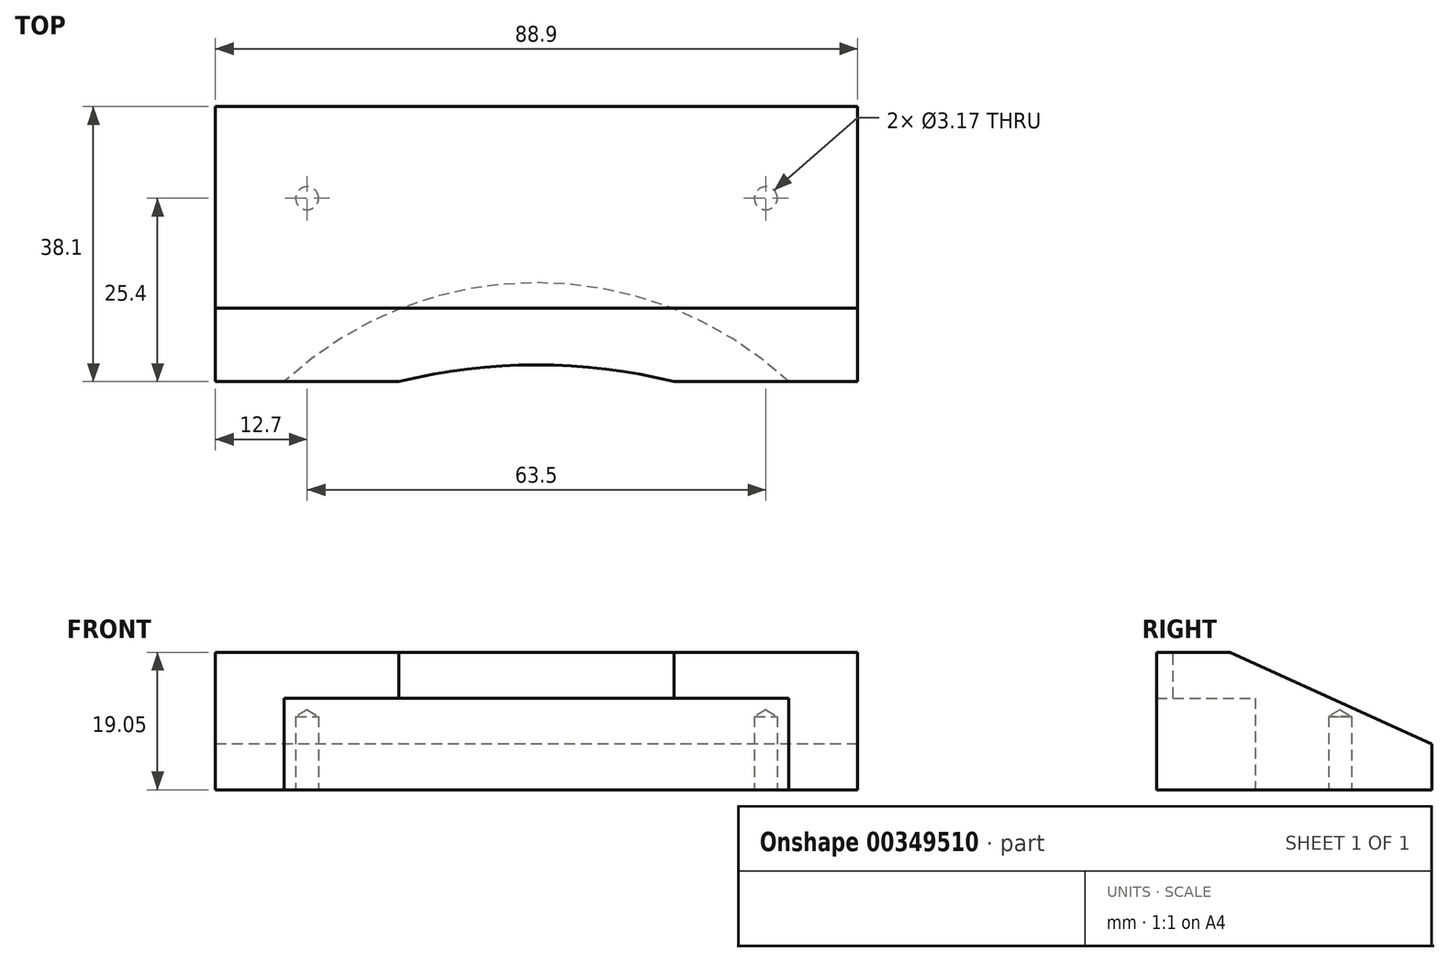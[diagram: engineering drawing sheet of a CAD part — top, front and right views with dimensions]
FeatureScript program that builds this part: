
annotation { "Feature Type Name" : "Feature", "Feature Type Description" : "" }
export const myFeature = defineFeature(function(context is Context, id is Id, definition is map)
    precondition{}
    {
        {
            var Q0;
            Q0=qCreatedBy(makeId("Top.planeOp"),FACE);
            var sketch = newSketch(context, id + "F0", { "sketchPlane" : qUnion([Q0])});
            skLineSegment(sketch, "E0.bottom", {"start": v(44.45, 19.05) * mm, "end": v(-44.45, 19.05) * mm});
            skLineSegment(sketch, "E0.top", {"start": v(44.45, -19.05) * mm, "end": v(-44.45, -19.05) * mm});
            skLineSegment(sketch, "E0.left", {"start": v(44.45, 19.05) * mm, "end": v(44.45, -19.05) * mm});
            skLineSegment(sketch, "E0.right", {"start": v(-44.45, 19.05) * mm, "end": v(-44.45, -19.05) * mm});
            skPoint(sketch, "E0.middle", {"position": v(0, 0) * mm});
            skSolve(sketch);
        }
        {
            var Q0;
            Q0=makeQuery(id+"F0.imprint","IMPRINT",FACE,{"disambiguationData":[TD([[makeQuery(id+"F0.imprint","IMPRINT",EDGE,{"derivedFrom":sQuery(id+"F0.wireOp",EDGE,"E0.bottom")}),1.0]])]});
            extrude(context, id + "F1", {"entities" : qUnion([Q0]), "depth" : 19.05 * mm});
        }
        {
            var Q0;
            Q0=makeQuery(id+"F1.opExtrude","SWEPT_FACE",FACE,{"disambiguationData":[OSD([sQuery(id+"F0.wireOp",EDGE,"E0.right")])]});
            var sketch = newSketch(context, id + "F2", { "sketchPlane" : qUnion([Q0])});
            skLineSegment(sketch, "E1", {"start": v(-19.05, 0) * mm, "end": v(-19.05, 6.35) * mm});
            skLineSegment(sketch, "E2", {"start": v(19.05, 19.05) * mm, "end": v(8.9, 19.05) * mm});
            skLineSegment(sketch, "E3", {"start": v(8.89, 19.05) * mm, "end": v(-19.05, 6.35) * mm});
            skLineSegment(sketch, "E4", {"start": v(-19.05, 6.35) * mm, "end": v(-19.05, 19.05) * mm});
            skLineSegment(sketch, "E5", {"start": v(-19.05, 19.05) * mm, "end": v(8.9, 19.05) * mm});
            skSolve(sketch);
        }
        {
            var Q0;
            Q0=makeQuery(id+"F2.imprint","IMPRINT",FACE,{"disambiguationData":[TD([[makeQuery(id+"F2.imprint","IMPRINT",EDGE,{"derivedFrom":sQuery(id+"F2.wireOp",EDGE,"E3")}),-1.0]])]});
            extrude(context, id + "F3", {"entities" : qUnion([Q0]), "operationType" : NewBodyOperationType.REMOVE, "oppositeDirection" : true, "depth" : 88.9 * mm});
        }
        {
            var Q0;
            Q0=makeQuery(id+"F1.opExtrude","CAP_FACE",FACE,{"disambiguationData":[OSD([sQuery(id+"F0.wireOp",EDGE,"E0.bottom"),sQuery(id+"F0.wireOp",EDGE,"E0.top"),sQuery(id+"F0.wireOp",EDGE,"E0.left"),sQuery(id+"F0.wireOp",EDGE,"E0.right")])],"isStart":false});
            var sketch = newSketch(context, id + "F4", { "sketchPlane" : qUnion([Q0])});
            skLineSegment(sketch, "E6", {"start": v(-44.45, -19.05) * mm, "end": v(-19.05, -19.05) * mm});
            skLineSegment(sketch, "E7", {"start": v(44.45, -19.05) * mm, "end": v(19.05, -19.05) * mm});
            skArc(sketch, "E8", {"start": v(19.05, -19.05) * mm, "mid": v(0, -16.72) * mm, "end": v(-19.05, -19.05) * mm});
            skLineSegment(sketch, "E9", {"start": v(-19.05, -19.05) * mm, "end": v(19.05, -19.05) * mm});
            skSolve(sketch);
        }
        {
            var Q0;
            Q0=makeQuery(id+"F4.imprint","IMPRINT",FACE,{"disambiguationData":[TD([[makeQuery(id+"F4.imprint","IMPRINT",EDGE,{"derivedFrom":sQuery(id+"F4.wireOp",EDGE,"E8")}),1.0]])]});
            var Q1;
            Q1=sQuery(id+"F4.wireOp",EDGE,"E9");
            var Q2;
            Q2=sQuery(id+"F4.wireOp",EDGE,"E8");
            extrude(context, id + "F5", {"entities" : qUnion([Q0]), "operationType" : NewBodyOperationType.REMOVE, "surfaceEntities" : qUnion([Q1, Q2]), "oppositeDirection" : true, "depth" : 25.4 * mm});
        }
        {
            var Q0;
            Q0=makeQuery(id+"F1.opExtrude","CAP_FACE",FACE,{"disambiguationData":[OSD([sQuery(id+"F0.wireOp",EDGE,"E0.bottom"),sQuery(id+"F0.wireOp",EDGE,"E0.top"),sQuery(id+"F0.wireOp",EDGE,"E0.left"),sQuery(id+"F0.wireOp",EDGE,"E0.right")])],"isStart":true});
            var sketch = newSketch(context, id + "F6", { "sketchPlane" : qUnion([Q0])});
            skLineSegment(sketch, "E10", {"start": v(44.45, 19.05) * mm, "end": v(34.93, 19.05) * mm});
            skLineSegment(sketch, "E11", {"start": v(-44.45, 19.05) * mm, "end": v(-34.93, 19.05) * mm});
            skArc(sketch, "E12", {"start": v(-34.93, 19.05) * mm, "mid": v(0, 5.35) * mm, "end": v(34.93, 19.05) * mm});
            skLineSegment(sketch, "E13", {"start": v(34.93, 19.05) * mm, "end": v(-34.93, 19.05) * mm});
            skSolve(sketch);
        }
        {
            var Q0;
            {var subQ0=sQuery(id+"F6.wireOp",EDGE,"E12");Q0=makeQuery(id+"F6.imprint","IMPRINT",FACE,{"disambiguationData":[TD([[makeQuery(id+"F6.imprint","IMPRINT",EDGE,{"derivedFrom":subQ0}),1.0]])]});}
            extrude(context, id + "F7", {"entities" : qUnion([Q0]), "operationType" : NewBodyOperationType.REMOVE, "oppositeDirection" : true, "depth" : 12.7 * mm});
        }
        {
            var Q0;
            Q0=makeQuery(id+"F1.opExtrude","CAP_FACE",FACE,{"disambiguationData":[OSD([sQuery(id+"F0.wireOp",EDGE,"E0.bottom"),sQuery(id+"F0.wireOp",EDGE,"E0.top"),sQuery(id+"F0.wireOp",EDGE,"E0.left"),sQuery(id+"F0.wireOp",EDGE,"E0.right")])],"isStart":true});
            var sketch = newSketch(context, id + "F8", { "sketchPlane" : qUnion([Q0])});
            skLineSegment(sketch, "E14", {"start": v(44.45, -19.05) * mm, "end": v(31.75, -19.05) * mm});
            skLineSegment(sketch, "E15", {"start": v(31.75, -6.35) * mm, "end": v(31.75, -19.05) * mm});
            skLineSegment(sketch, "E16", {"start": v(-44.45, -19.05) * mm, "end": v(-31.75, -19.05) * mm});
            skLineSegment(sketch, "E17", {"start": v(-31.75, -6.35) * mm, "end": v(-31.75, -19.05) * mm});
            skCircle(sketch, "E18", {"center": v(31.75, -6.35) * mm, "radius": 1.59 * mm});
            skCircle(sketch, "E19", {"center": v(-31.75, -6.35) * mm, "radius": 1.59 * mm});
            skSolve(sketch);
        }
        {
            var Q0;
            Q0=sQuery(id+"F8.wireOp",VERTEX,"E18.center");
            var Q1;
            Q1=sQuery(id+"F8.wireOp",VERTEX,"E17.start");
            var Q2;
            Q2=makeQuery(id+"F1.opExtrude","SWEPT_BODY",BODY,{"disambiguationData":[OSD([sQuery(id+"F0.wireOp",EDGE,"E0.bottom"),sQuery(id+"F0.wireOp",EDGE,"E0.top"),sQuery(id+"F0.wireOp",EDGE,"E0.left"),sQuery(id+"F0.wireOp",EDGE,"E0.right")])]});
            hole(context, id + "F9", {"style" : HoleStyle.SIMPLE, "endStyle" : HoleEndStyle.BLIND, "holeDiameter" : 3.17 * mm, "holeDepth" : 10.16 * mm, "isTappedThrough" : true, "tappedDepth" : 12.7 * mm, "tapClearance" : 3, "locations" : qUnion([Q0, Q1]), "scope" : qUnion([Q2])});
        }
    });
